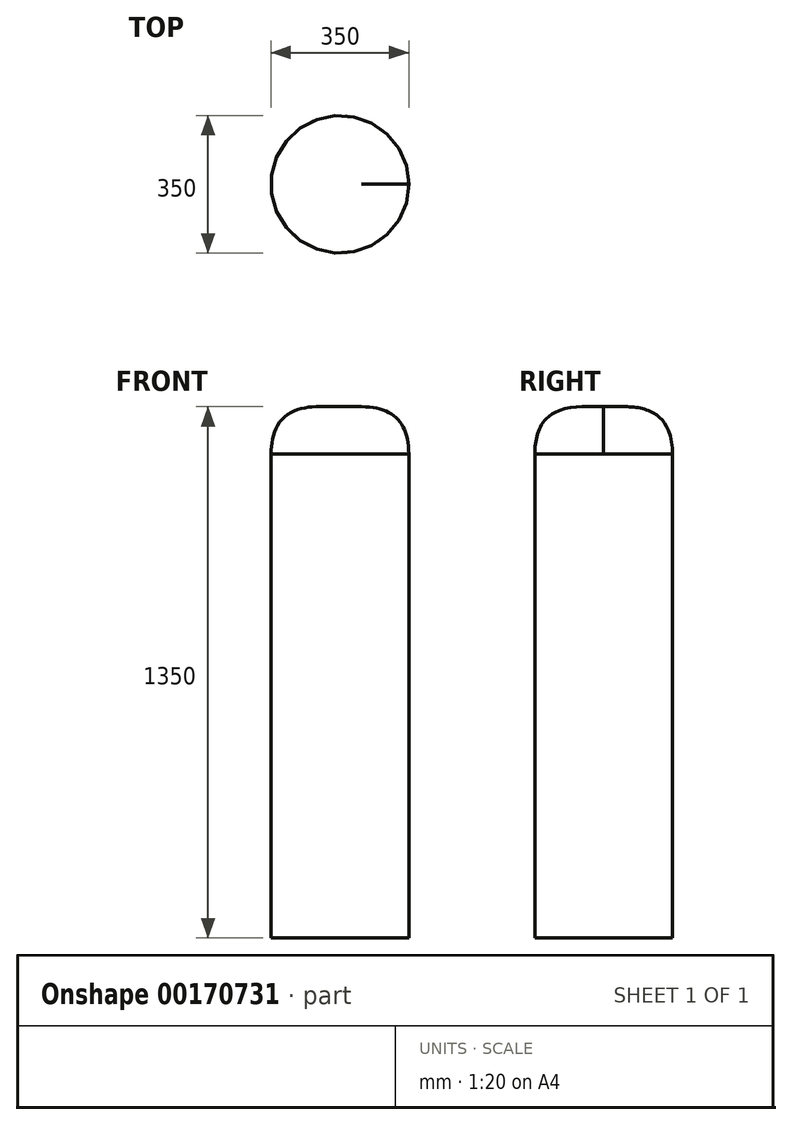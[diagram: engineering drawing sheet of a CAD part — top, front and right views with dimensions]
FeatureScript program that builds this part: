
annotation { "Feature Type Name" : "Feature", "Feature Type Description" : "" }
export const myFeature = defineFeature(function(context is Context, id is Id, definition is map)
    precondition{}
    {
        {
            var Q0;
            Q0=qCreatedBy(makeId("Top.planeOp"),FACE);
            var sketch = newSketch(context, id + "F0", { "sketchPlane" : qUnion([Q0])});
            skCircle(sketch, "E0", {"center": v(0, 0) * mm, "radius": 175 * mm});
            skSolve(sketch);
        }
        {
            var Q0;
            Q0 = qSketchRegion(id + "F0", true);
            extrude(context, id + "F1", {"entities" : qUnion([Q0]), "depth" : 1350 * mm});
        }
        {
            var Q0;
            Q0=makeQuery(id+"F1.opExtrude","CAP_EDGE",EDGE,{"disambiguationData":[OSD([sQuery(id+"F0.wireOp",EDGE,"E0")])],"isStart":false});
            fillet(context, id + "F2", {"entities" : qUnion([Q0]), "radius" : 120 * mm, "tangentPropagation" : true, "rho" : 0.5, "crossSection" : FilletCrossSection.CONIC, "allowEdgeOverflow" : false});
        }
    });
